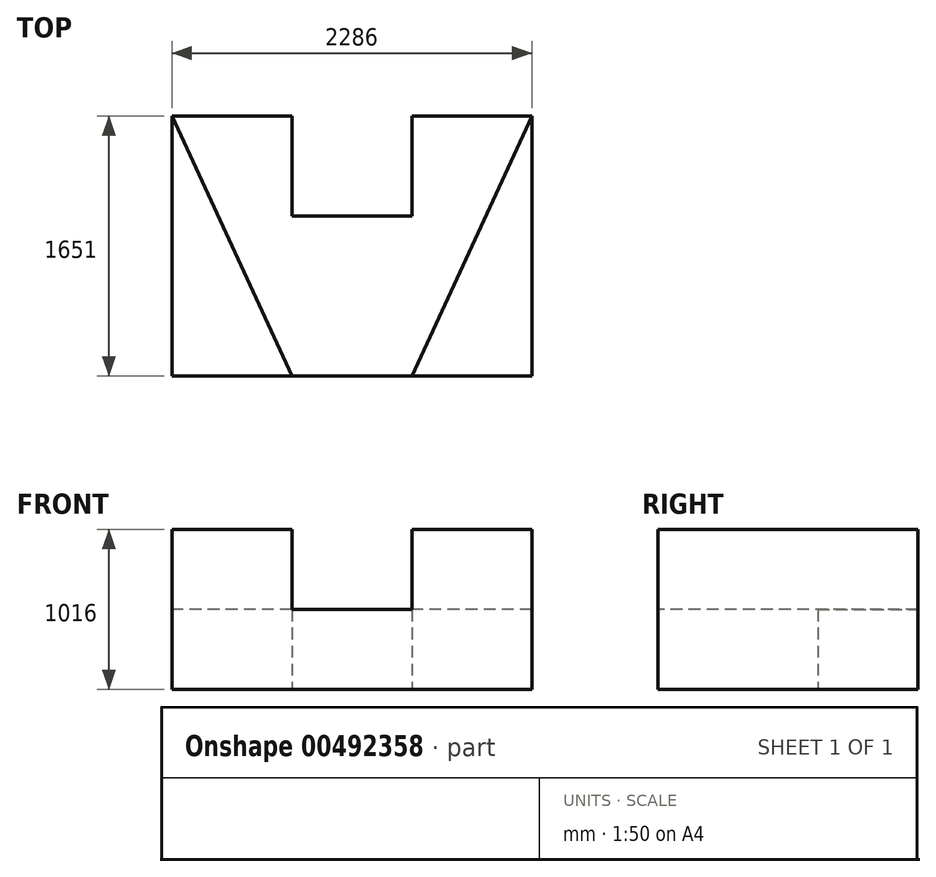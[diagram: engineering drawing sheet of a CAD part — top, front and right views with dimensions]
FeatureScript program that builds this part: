
annotation { "Feature Type Name" : "Feature", "Feature Type Description" : "" }
export const myFeature = defineFeature(function(context is Context, id is Id, definition is map)
    precondition{}
    {
        {
            var Q0;
            Q0=qCreatedBy(makeId("Top.planeOp"),FACE);
            var sketch = newSketch(context, id + "F0", { "sketchPlane" : qUnion([Q0])});
            skLineSegment(sketch, "E0.bottom", {"start": v(1143, -825.5) * mm, "end": v(-1143, -825.5) * mm});
            skLineSegment(sketch, "E0.top", {"start": v(1143, 825.5) * mm, "end": v(381, 825.5) * mm});
            skLineSegment(sketch, "E0.left", {"start": v(1143, -825.5) * mm, "end": v(1143, 825.5) * mm});
            skLineSegment(sketch, "E0.right", {"start": v(-1143, -825.5) * mm, "end": v(-1143, 825.5) * mm});
            skPoint(sketch, "E0.middle", {"position": v(0, 0) * mm});
            skLineSegment(sketch, "E1", {"start": v(-381, 190.5) * mm, "end": v(381, 190.5) * mm});
            skLineSegment(sketch, "E2", {"start": v(-381, 825.5) * mm, "end": v(-381, 190.5) * mm});
            skLineSegment(sketch, "E3", {"start": v(381, 190.5) * mm, "end": v(381, 825.5) * mm});
            skLineSegment(sketch, "E4.trimOffspring", {"start": v(-381, 825.5) * mm, "end": v(-1143, 825.5) * mm});
            skPoint(sketch, "E5.end.orphan", {"position": v(0, 190.5) * mm});
            skPoint(sketch, "E6.orphan", {"position": v(0, 825.5) * mm});
            skPoint(sketch, "E7.orphan", {"position": v(-1143, 190.5) * mm});
            skPoint(sketch, "E8.orphan", {"position": v(1143, 190.5) * mm});
            skSolve(sketch);
        }
        {
            var Q0;
            Q0=makeQuery(id+"F0.imprint","IMPRINT",FACE,{"disambiguationData":[TD([[makeQuery(id+"F0.imprint","IMPRINT",EDGE,{"derivedFrom":sQuery(id+"F0.wireOp",EDGE,"E0.bottom")}),-1.0]])]});
            extrude(context, id + "F1", {"entities" : qUnion([Q0]), "depth" : 508 * mm, "offsetDistance" : 25.4 * mm});
        }
        {
            var Q0;
            Q0=makeQuery(id+"F1.opExtrude","CAP_FACE",FACE,{"disambiguationData":[OSD([sQuery(id+"F0.wireOp",EDGE,"E0.bottom"),sQuery(id+"F0.wireOp",EDGE,"E0.top"),sQuery(id+"F0.wireOp",EDGE,"E0.left"),sQuery(id+"F0.wireOp",EDGE,"E0.right"),sQuery(id+"F0.wireOp",EDGE,"E2"),sQuery(id+"F0.wireOp",EDGE,"E1"),sQuery(id+"F0.wireOp",EDGE,"E3"),sQuery(id+"F0.wireOp",EDGE,"E4.trimOffspring")])],"isStart":false});
            var sketch = newSketch(context, id + "F2", { "sketchPlane" : qUnion([Q0])});
            skLineSegment(sketch, "E9", {"start": v(-1143, -825.5) * mm, "end": v(-381, -825.5) * mm});
            skLineSegment(sketch, "E10", {"start": v(-381, -825.5) * mm, "end": v(381, -825.5) * mm});
            skLineSegment(sketch, "E11", {"start": v(1143, -825.5) * mm, "end": v(381, -825.5) * mm});
            skLineSegment(sketch, "E12", {"start": v(-1143, 825.5) * mm, "end": v(-381, -825.5) * mm});
            skLineSegment(sketch, "E13", {"start": v(1143, 825.5) * mm, "end": v(381, -825.5) * mm});
            skSolve(sketch);
        }
        {
            var Q0;
            Q0=makeQuery(id+"F2.imprint","IMPRINT",FACE,{"disambiguationData":[TD([[makeQuery(id+"F2.imprint","IMPRINT",EDGE,{"derivedFrom":sQuery(id+"F2.wireOp",EDGE,"E9")}),-1.0]])]});
            var Q1;
            Q1=makeQuery(id+"F2.imprint","IMPRINT",FACE,{"disambiguationData":[TD([[makeQuery(id+"F2.imprint","IMPRINT",EDGE,{"derivedFrom":sQuery(id+"F2.wireOp",EDGE,"E11")}),-1.0]])]});
            extrude(context, id + "F3", {"entities" : qUnion([Q0, Q1]), "operationType" : NewBodyOperationType.ADD, "depth" : 508 * mm, "offsetDistance" : 25.4 * mm});
        }
    });
